# Revit family: Electrical_Equipment-Floor_Box-Hubbell_Wiring-System_One-S1SFB
name_source: partatom
category: Electrical Fixtures
revit_build: Autodesk Revit 2015 (Build: 20140606_1530(x64)
units: mm (PartAtom-declared; Revit-internal decimal feet)

## types (3) — shared parameters
Apparent Load = 4800 VA
Assembly Code = D5020115
Conduit Connector 1 Description = Power Conduit Connector 1
Conduit Connector 2 Description = Power Conduit Connector 2
Conduit Connector 3 Description = Data Conduit Connector 1
Conduit Connector 4 Description = Data Conduit Connector 2
Cover Material = Metal-Hubbell-Aluminum
Default Elevation = 0' - 0"
Description = System One - 4" Floor Box
Electrical Connector Description = Power Connector
Load Classification = Power
Manufacturer = Hubbell-Wiring
Number of Poles = 1
Power Factor = 1
Product Documentation Link = http://ecatalog.hubbell-wiring.com
Product Page URL = http://ecatalog.hubbell-wiring.com
Product data url = https://bimobject.com
Subplate = Subplate : Abandonment Plate
URL = http://www.hubbell-wiring.com
Voltage = 120 V

## per-type parameters (varying)
| type | Hardware Material | Model |
| Steel | Metal-Hubbell-Steel | S1SFB |
| Cast Iron | Metal-Hubbell-Cast Iron | S1CFB |
| Steel AV | Metal-Hubbell-Steel AV | S1SFBAV |

## geometry (parser evidence)
native form markers: Blend x33, Sweep x6
no freeform markers — native parametric forms only
